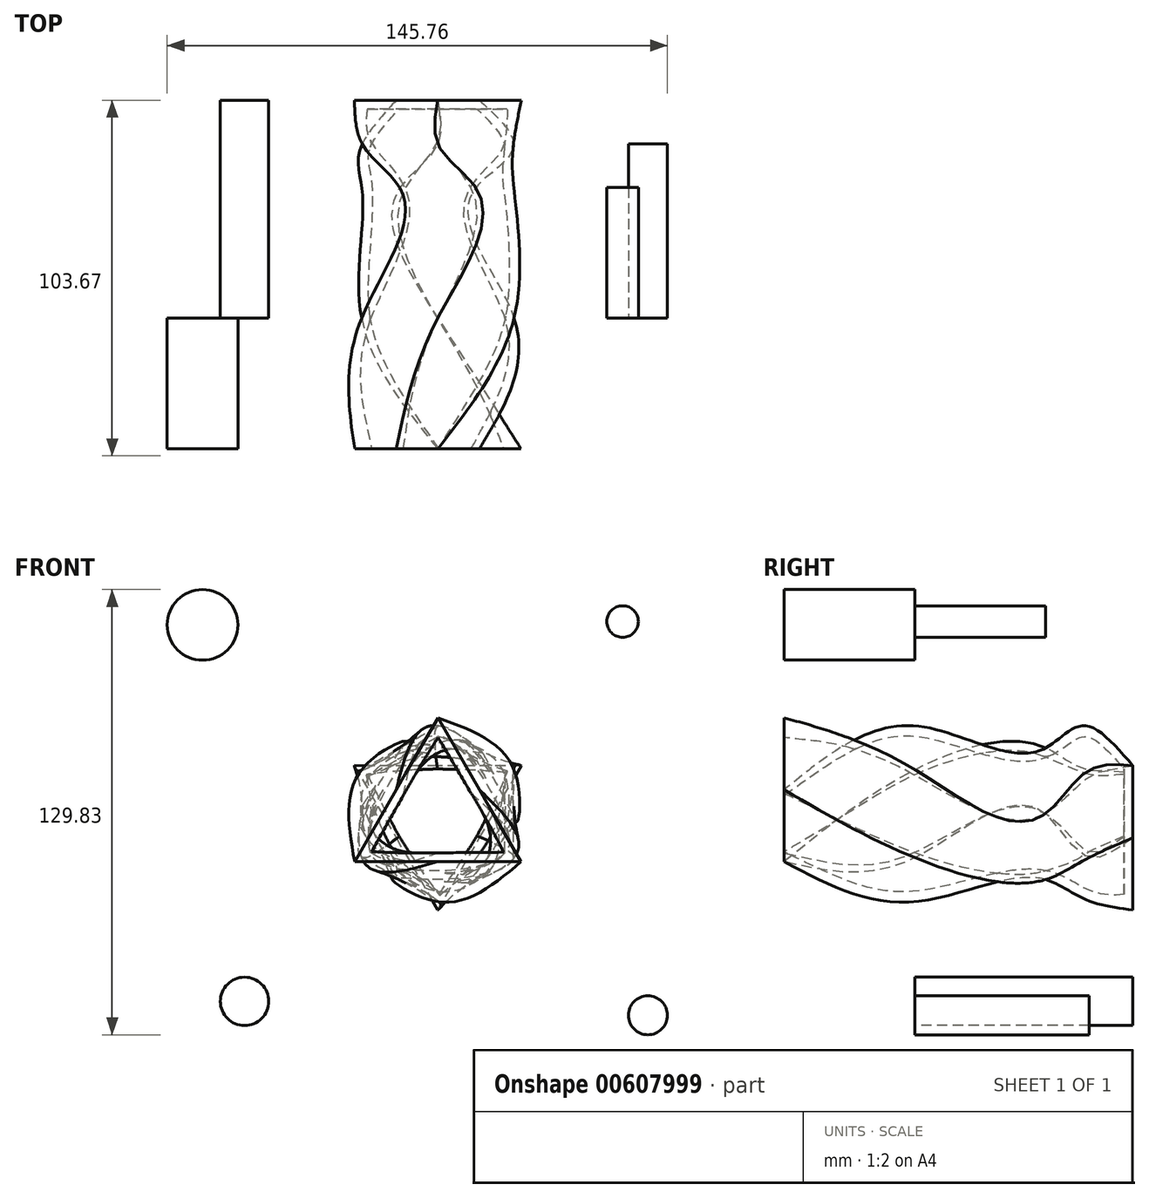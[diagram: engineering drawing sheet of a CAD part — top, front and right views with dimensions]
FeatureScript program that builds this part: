
annotation { "Feature Type Name" : "Feature", "Feature Type Description" : "" }
export const myFeature = defineFeature(function(context is Context, id is Id, definition is map)
    precondition{}
    {
        {
            var Q0;
            Q0=qCreatedBy(makeId("Front.planeOp"),FACE);
            var sketch = newSketch(context, id + "F0", { "sketchPlane" : qUnion([Q0])});
            skPoint(sketch, "E0.0.midPoint", {"position": v(22.2, 0) * mm});
            skPoint(sketch, "E0.cCircle.center.orphan", {"position": v(0, 0) * mm});
            skCircle(sketch, "E1.cCircle", {"center": v(0, 0) * mm, "radius": 22.2 * mm, "construction": true});
            skLineSegment(sketch, "E1.0", {"start": v(22.2, 12.82) * mm, "end": v(22.2, -12.82) * mm});
            skLineSegment(sketch, "E1.1", {"start": v(22.2, -12.82) * mm, "end": v(0, -25.64) * mm});
            skLineSegment(sketch, "E1.2", {"start": v(0, -25.64) * mm, "end": v(-22.2, -12.82) * mm});
            skLineSegment(sketch, "E1.3", {"start": v(-22.2, -12.82) * mm, "end": v(-22.2, 12.82) * mm});
            skLineSegment(sketch, "E1.4", {"start": v(-22.2, 12.82) * mm, "end": v(0, 25.64) * mm});
            skLineSegment(sketch, "E1.5", {"start": v(0, 25.64) * mm, "end": v(22.2, 12.82) * mm});
            skSolve(sketch);
        }
        {
            var Q0;
            Q0=qCreatedBy(makeId("Front.planeOp"),FACE);
            var sketch = newSketch(context, id + "F1", { "sketchPlane" : qUnion([Q0])});
            skCircle(sketch, "E2", {"center": v(-68.57, 55.09) * mm, "radius": 10.3 * mm});
            skSolve(sketch);
        }
        {
            var Q0;
            Q0 = qSketchRegion(id + "F1", true);
            extrude(context, id + "F2", {"entities" : qUnion([Q0]), "depth" : 38.1 * mm, "offsetDistance" : 25.4 * mm});
        }
        {
            var Q0;
            Q0=makeQuery(id+"F2.opExtrude","CAP_FACE",FACE,{"disambiguationData":[OSD([sQuery(id+"F1.wireOp",EDGE,"E2")])],"isStart":false});
            var sketch = newSketch(context, id + "F3", { "sketchPlane" : qUnion([Q0])});
            skCircle(sketch, "E3.cCircle", {"center": v(0, 0) * mm, "radius": 13.99 * mm, "construction": true});
            skLineSegment(sketch, "E3.0", {"start": v(0.03, 27.98) * mm, "end": v(24.22, -14.01) * mm});
            skLineSegment(sketch, "E3.1", {"start": v(24.22, -14.01) * mm, "end": v(-24.25, -13.97) * mm});
            skLineSegment(sketch, "E3.2", {"start": v(-24.25, -13.97) * mm, "end": v(0.03, 27.98) * mm});
            skPoint(sketch, "E3.0.midPoint", {"position": v(12.12, 6.98) * mm});
            skSolve(sketch);
        }
        {
            var Q0;
            Q0=qCreatedBy(makeId("Front.planeOp"),FACE);
            var sketch = newSketch(context, id + "F4", { "sketchPlane" : qUnion([Q0])});
            skCircle(sketch, "E4", {"center": v(53.85, 56.06) * mm, "radius": 4.6 * mm});
            skSolve(sketch);
        }
        {
            var Q0;
            Q0 = qSketchRegion(id + "F4", true);
            extrude(context, id + "F5", {"entities" : qUnion([Q0]), "oppositeDirection" : true, "depth" : 38.1 * mm, "offsetDistance" : 25.4 * mm});
        }
        {
            var Q0;
            Q0=makeQuery(id+"F5.opExtrude","CAP_FACE",FACE,{"disambiguationData":[OSD([sQuery(id+"F4.wireOp",EDGE,"E4")])],"isStart":false});
            var sketch = newSketch(context, id + "F6", { "sketchPlane" : qUnion([Q0])});
            skPoint(sketch, "E5.cCircle.center.orphan", {"position": v(0, 0) * mm});
            skCircle(sketch, "E6.cCircle", {"center": v(0, 0) * mm, "radius": 19.19 * mm, "construction": true});
            skLineSegment(sketch, "E6.0", {"start": v(-22.16, 0.04) * mm, "end": v(-11.05, 19.2) * mm});
            skLineSegment(sketch, "E6.1", {"start": v(-11.05, 19.2) * mm, "end": v(11.11, 19.17) * mm});
            skLineSegment(sketch, "E6.2", {"start": v(11.11, 19.17) * mm, "end": v(22.16, -0.04) * mm});
            skLineSegment(sketch, "E6.3", {"start": v(22.16, -0.04) * mm, "end": v(11.05, -19.2) * mm});
            skLineSegment(sketch, "E6.4", {"start": v(11.05, -19.2) * mm, "end": v(-11.11, -19.17) * mm});
            skLineSegment(sketch, "E6.5", {"start": v(-11.11, -19.17) * mm, "end": v(-22.16, 0.04) * mm});
            skPoint(sketch, "E6.0.midPoint", {"position": v(-16.6, 9.62) * mm});
            skSolve(sketch);
        }
        {
            var Q0;
            Q0=qCreatedBy(makeId("Front.planeOp"),FACE);
            var sketch = newSketch(context, id + "F7", { "sketchPlane" : qUnion([Q0])});
            skCircle(sketch, "E7", {"center": v(61.22, -58.77) * mm, "radius": 5.68 * mm});
            skSolve(sketch);
        }
        {
            var Q0;
            Q0 = qSketchRegion(id + "F7", true);
            extrude(context, id + "F8", {"entities" : qUnion([Q0]), "oppositeDirection" : true, "depth" : 50.8 * mm, "offsetDistance" : 25.4 * mm});
        }
        {
            var Q0;
            Q0=makeQuery(id+"F8.opExtrude","CAP_FACE",FACE,{"disambiguationData":[OSD([sQuery(id+"F7.wireOp",EDGE,"E7")])],"isStart":false});
            var sketch = newSketch(context, id + "F9", { "sketchPlane" : qUnion([Q0])});
            skCircle(sketch, "E8.cCircle", {"center": v(0, 0) * mm, "radius": 22.04 * mm, "construction": true});
            skLineSegment(sketch, "E8.0", {"start": v(-22.04, -12.73) * mm, "end": v(-22.04, 12.73) * mm});
            skLineSegment(sketch, "E8.1", {"start": v(-22.04, 12.73) * mm, "end": v(0, 25.45) * mm});
            skLineSegment(sketch, "E8.2", {"start": v(0, 25.45) * mm, "end": v(22.04, 12.73) * mm});
            skLineSegment(sketch, "E8.3", {"start": v(22.04, 12.73) * mm, "end": v(22.04, -12.73) * mm});
            skLineSegment(sketch, "E8.4", {"start": v(22.04, -12.73) * mm, "end": v(0, -25.45) * mm});
            skLineSegment(sketch, "E8.5", {"start": v(0, -25.45) * mm, "end": v(-22.04, -12.73) * mm});
            skPoint(sketch, "E8.0.midPoint", {"position": v(-22.04, 0) * mm});
            skSolve(sketch);
        }
        {
            var Q0;
            Q0=qCreatedBy(makeId("Front.planeOp"),FACE);
            var sketch = newSketch(context, id + "F10", { "sketchPlane" : qUnion([Q0])});
            skCircle(sketch, "E9", {"center": v(-56.32, -54.7) * mm, "radius": 7.06 * mm});
            skSolve(sketch);
        }
        {
            var Q0;
            Q0 = qSketchRegion(id + "F10", true);
            extrude(context, id + "F11", {"entities" : qUnion([Q0]), "oppositeDirection" : true, "depth" : 63.5 * mm, "offsetDistance" : 25.4 * mm});
        }
        {
            var Q0;
            Q0=makeQuery(id+"F11.opExtrude","CAP_FACE",FACE,{"disambiguationData":[OSD([sQuery(id+"F10.wireOp",EDGE,"E9")])],"isStart":false});
            var sketch = newSketch(context, id + "F12", { "sketchPlane" : qUnion([Q0])});
            skCircle(sketch, "E10.cCircle", {"center": v(0, 0) * mm, "radius": 14.04 * mm, "construction": true});
            skLineSegment(sketch, "E10.0", {"start": v(24.3, 14.05) * mm, "end": v(0.02, -28.07) * mm});
            skLineSegment(sketch, "E10.1", {"start": v(0.02, -28.07) * mm, "end": v(-24.32, 14.02) * mm});
            skLineSegment(sketch, "E10.2", {"start": v(-24.32, 14.02) * mm, "end": v(24.3, 14.05) * mm});
            skPoint(sketch, "E10.0.midPoint", {"position": v(12.16, -7.01) * mm});
            skSolve(sketch);
        }
        {
            var Q0;
            Q0=makeQuery(id+"F12.imprint","IMPRINT",FACE,{"disambiguationData":[TD([[makeQuery(id+"F12.imprint","IMPRINT",EDGE,{"derivedFrom":sQuery(id+"F12.wireOp",EDGE,"E10.0")}),-1.0]])]});
            var Q1;
            Q1=makeQuery(id+"F9.imprint","IMPRINT",FACE,{"disambiguationData":[TD([[makeQuery(id+"F9.imprint","IMPRINT",EDGE,{"derivedFrom":sQuery(id+"F9.wireOp",EDGE,"E8.0")}),-1.0]])]});
            var Q2;
            Q2=makeQuery(id+"F6.imprint","IMPRINT",FACE,{"disambiguationData":[TD([[makeQuery(id+"F6.imprint","IMPRINT",EDGE,{"derivedFrom":sQuery(id+"F6.wireOp",EDGE,"E6.0")}),-1.0]])]});
            var Q3;
            Q3=makeQuery(id+"F0.imprint","IMPRINT",FACE,{"disambiguationData":[TD([[makeQuery(id+"F0.imprint","IMPRINT",EDGE,{"derivedFrom":sQuery(id+"F0.wireOp",EDGE,"E1.0")}),-1.0]])]});
            var Q4;
            Q4=makeQuery(id+"F3.imprint","IMPRINT",FACE,{"disambiguationData":[TD([[makeQuery(id+"F3.imprint","IMPRINT",EDGE,{"derivedFrom":sQuery(id+"F3.wireOp",EDGE,"E3.0")}),-1.0]])]});
            loft(context, id + "F13", {"sheetProfilesArray" : [{ "sheetProfileEntities" : qUnion([Q0]) }, { "sheetProfileEntities" : qUnion([Q1]) }, { "sheetProfileEntities" : qUnion([Q2]) }, { "sheetProfileEntities" : qUnion([Q3]) }, { "sheetProfileEntities" : qUnion([Q4]) }]});
        }
        {
            var Q0;
            Q0=makeQuery(id+"F13.opLoft","CAP_FACE",FACE,{"disambiguationData":[OSD([makeQuery(id+"F3.imprint","IMPRINT",FACE,{"disambiguationData":[TD([[makeQuery(id+"F3.imprint","IMPRINT",EDGE,{"derivedFrom":sQuery(id+"F3.wireOp",EDGE,"E3.0")}),-1.0]])]})])],"isStart":true});
            shell(context, id + "F14", {"entities" : qUnion([Q0]), "thickness" : 2.54 * mm});
        }
    });
